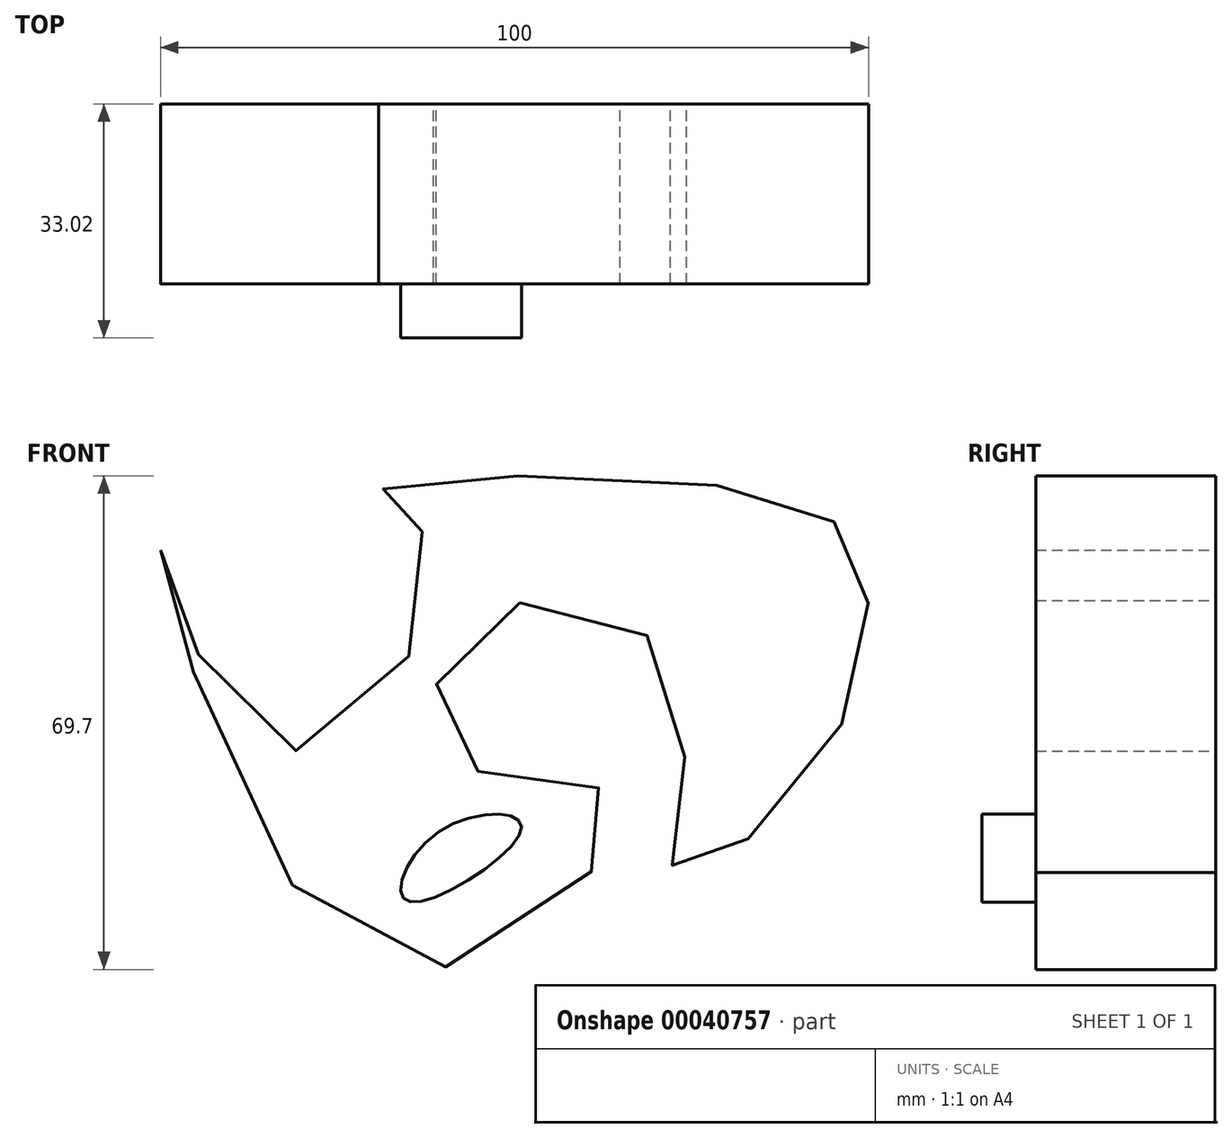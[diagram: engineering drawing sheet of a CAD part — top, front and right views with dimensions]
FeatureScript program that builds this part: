
annotation { "Feature Type Name" : "Feature", "Feature Type Description" : "" }
export const myFeature = defineFeature(function(context is Context, id is Id, definition is map)
    precondition{}
    {
        {
            var Q0;
            Q0=qCreatedBy(makeId("Front.planeOp"),FACE);
            var sketch = newSketch(context, id + "F0", { "sketchPlane" : qUnion([Q0])});
            skFitSpline(sketch, "E0", {"points": [v(-51, 44.98) * mm, v(-19.9, -13.31) * mm, v(13.73, 9.1) * mm, v(-9.25, 15.27) * mm, v(-5.6, 35.45) * mm, v(22.14, 27.04) * mm, v(21.58, 0) * mm, v(42.04, 15) * mm, v(47.92, 43.3) * mm, v(30.83, 53.67) * mm, v(-20.18, 53.1) * mm, v(-12.33, 44.14) * mm, v(-34.75, 16.95) * mm, v(-51, 44.98) * mm]});
            skSolve(sketch);
        }
        {
            var Q0;
            Q0=makeQuery(id+"F0.imprint","IMPRINT",FACE,{"disambiguationData":[TD([[makeQuery(id+"F0.imprint","IMPRINT",EDGE,{"derivedFrom":sQuery(id+"F0.wireOp",EDGE,"E0")}),1.0]])]});
            extrude(context, id + "F1", {"entities" : qUnion([Q0]), "depth" : 25.4 * mm});
        }
        {
            var Q0;
            Q0=makeQuery(id+"F1.opExtrude","CAP_FACE",FACE,{"disambiguationData":[OSD([sQuery(id+"F0.wireOp",EDGE,"E0")])],"isStart":false});
            var sketch = newSketch(context, id + "F2", { "sketchPlane" : qUnion([Q0])});
            skFitSpline(sketch, "E1", {"points": [v(-11.77, 5.18) * mm, v(-15.97, -4.62) * mm, v(0, 5.75) * mm, v(-11.77, 5.18) * mm]});
            skSolve(sketch);
        }
        {
            var Q0;
            Q0=makeQuery(id+"F2.imprint","IMPRINT",FACE,{"disambiguationData":[TD([[makeQuery(id+"F2.imprint","IMPRINT",EDGE,{"derivedFrom":sQuery(id+"F2.wireOp",EDGE,"E1")}),1.0]])]});
            extrude(context, id + "F3", {"entities" : qUnion([Q0]), "operationType" : NewBodyOperationType.ADD, "depth" : 7.62 * mm});
        }
    });
